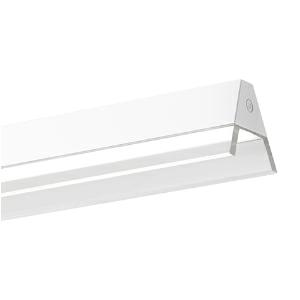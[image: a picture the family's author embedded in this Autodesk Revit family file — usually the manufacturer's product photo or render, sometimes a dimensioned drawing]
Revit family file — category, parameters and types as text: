
# Revit family: 3f_filippi_-_3f_mirella_di_sp_3f_filippi_-_10924_-_3f_mirella_wh_di_40_8_sp_l1480_b56e
name_source: partatom
category: Lighting Fixtures
units: mm (PartAtom-declared; Revit-internal decimal feet)

## family parameters
Cut with Voids When Loaded = No
Host = Face
Light Source = No
Part Type = Normal
Room Calculation Point = No
Round Connector Dimension = Use Diameter
Shared = No

## types (1)
- 3F Filippi - 3F Mirella DI SP (1 x LED, 5849 lm, 58 W, 4000 K)
    Apparent Load = 58 VA
    Approval mark = ENEC
    CIE Flux Codes = 62 95 99 79 100
    Color Rendering = 80
    Color Temperature = 4000 K
    Control Gear = Electronic ballast
    Default Elevation = 1800 mm
    Description = ILLUMINOTECHNICAL
Luminous efficiency 100% (DLOR 79%, ULOR 21%).
Initial luminous flux of the luminaire 5849 lm.
Symmetric direct-indirect distribution.
Installation Interdistance Transv.D = 1.65 x hu - Long.D = 1.26 x hu.
Average luminance <3000 cd/m² for radial angles >65°.
Tabular UGR (CIE 117 - 4H-8H; S=0.25H; 70/50/20): RUG 16.3 - 17.4.
Beam angle: 89° - 96°.
Luminous efficacy 101 lm/W.
Lifetime (L93/B10): 30000 h. (tq+25°C)
Lifetime (L90/B10): 50000 h. (tq+25°C)
Lifetime (L85/B10): 80000 h. (tq+25°C)
Lifetime (L80/B10): 100000 h. (tq+25°C)
Sudden decreased luminous flux after 50000 hours: 0% (C0).
Photobiological safety in compliance with IEC/TR 62778: RG0 risk exempt, (IEC 62471).
In compliance with IEC/EN 62722-2-1 - IEC/EN 62717 standards.

SOURCE
One 40W/840 linear LED module for direct lighting + one 8W/840 linear LED module for indirect lighting.
Energy efficiency class (UE 2019/2020 - UE 2019/2015): D, E.
CIE 13.3 Colour rendering index: CRI >80 (R9 <50%).
IES TM-30 Fidelity Index: Rf = 84 Rg = 95.
CCT nominal colour temperature 4000 K.
Colour initial tolerance (MacAdam): SDCM 3.

MECHANICAL
Housing in white painted extruded aluminium.
Methacrylate (PMMA) primary lens for total source shielding.
Highly aesthetic external lens in transparent methacrylate (PMMA) for optimizing light distribution.
Flat transparent prismatic methacrylate (PMMA) filter, multi-lenticular exterior, anti-glare.
Upper film in translucent polycarbonate, self-extinguishing, UV stabilised.
White painted aluminium end caps.
Luminaire with limited surface temperature. - D - (EN 60598-2-24)
Dimensions: 1480x112 mm, height 91 mm. Weight 5.95 kg.
IP40 protection degree.
Mechanical strength to impacts IK06 (1 joule).
Glow-wire test resistance 650°C.

ELECTRICAL
Halogen Free electronic wiring 230V-50/60Hz, power factor 0.95, THD <25%, constant output current, SELV, class I, 2 driver.
Power of the luminaire 58 W.
CE - IEC 60598-1 - EN 60598-1.
SAFE FLICKER: PstLM=<1 and SVM=<0.4 (IEC TR 61547-1 and IEC TR 63158), to ensure a more comfortable and safe light.
Luminaire compliant with EN 60598-2-22 for power supply from a centralised emergency system CPSS (Central Power Supply System), not incorporated in the luminaire - high risk areas excluded. The default power and flux are 100% in AC and 100% in DC.
Ambient temperature from 0°C to +25°C.
Temperature class T6 max 85°C.
Relative humidity UR: <85%.

INSTALLATION
Suspended.

SUPPLIED
Suspensions with chrome bosses and quick adjusters, 2 m galvanised steel cable.
Transparent 2.3 m 3x0.75 mm² power cable with white power supply case for mounting on the ceiling.

APPLICATIONS
Environments involving accurate visual tasks where a diffused and soft light for an optimum visual comfort and the source total shielding are required.
In environments with VDTs, managerial offices and staterooms.

WARNING
Luminaire designed for disposal/recycling at end-of-life.
Replaceable (LED only) light source by a professional. Replaceable control gear by a professional.
    Height = 91 mm
    Lamp = 1 x LED
    Lamp Light Flux = 5849 lm
    Lamp Power = 58 W
    Lamp count = 1
    Length = 1480 mm
    Lifetime = 50000 h
    Luminous efficacy = 101 lm/W
    Manufacturer = 3F Filippi
    ModVariant = No
    Model = 3F Filippi - 10924 - 3F Mirella WH DI 40+8 SP L1480
    Mounting Place = Ceiling
    Mounting Type = Pendant
    Number of Poles = 1
    OnlyDefault = Yes
    Power Factor = 1
    Product Name = 3F Filippi - 3F Mirella DI SP
    Product group = pendant luminaire
    ProductGroupID = 9
    Protection Class = Protection class I
    Protection Degree = IP 40
    RLX_Detail_Level = 1
    RLX_Emergency_Light_Flux = 0 lm
    RLX_Emergency_Type = 0
    RLX_Emergency_Type_DB = No
    RlxData = <blob elided: 64161 chars, md5=325c64fb>
    Socket = socket
    Standby Power = 0 W
    System Light Flux = 5849 lm
    System Power = 58 W
    Type Comments = Product without accessories
    Type Image = 3ffilippi_3f_mirella_wh.jpg
    URL = http://relux.com
    VarID = ---
    Voltage = 0 V
    Weight = 0.00 kg
    Width = 112 mm

## geometry (parser evidence)
native form markers: Blend x4, Sweep x13
no freeform markers — native parametric forms only
